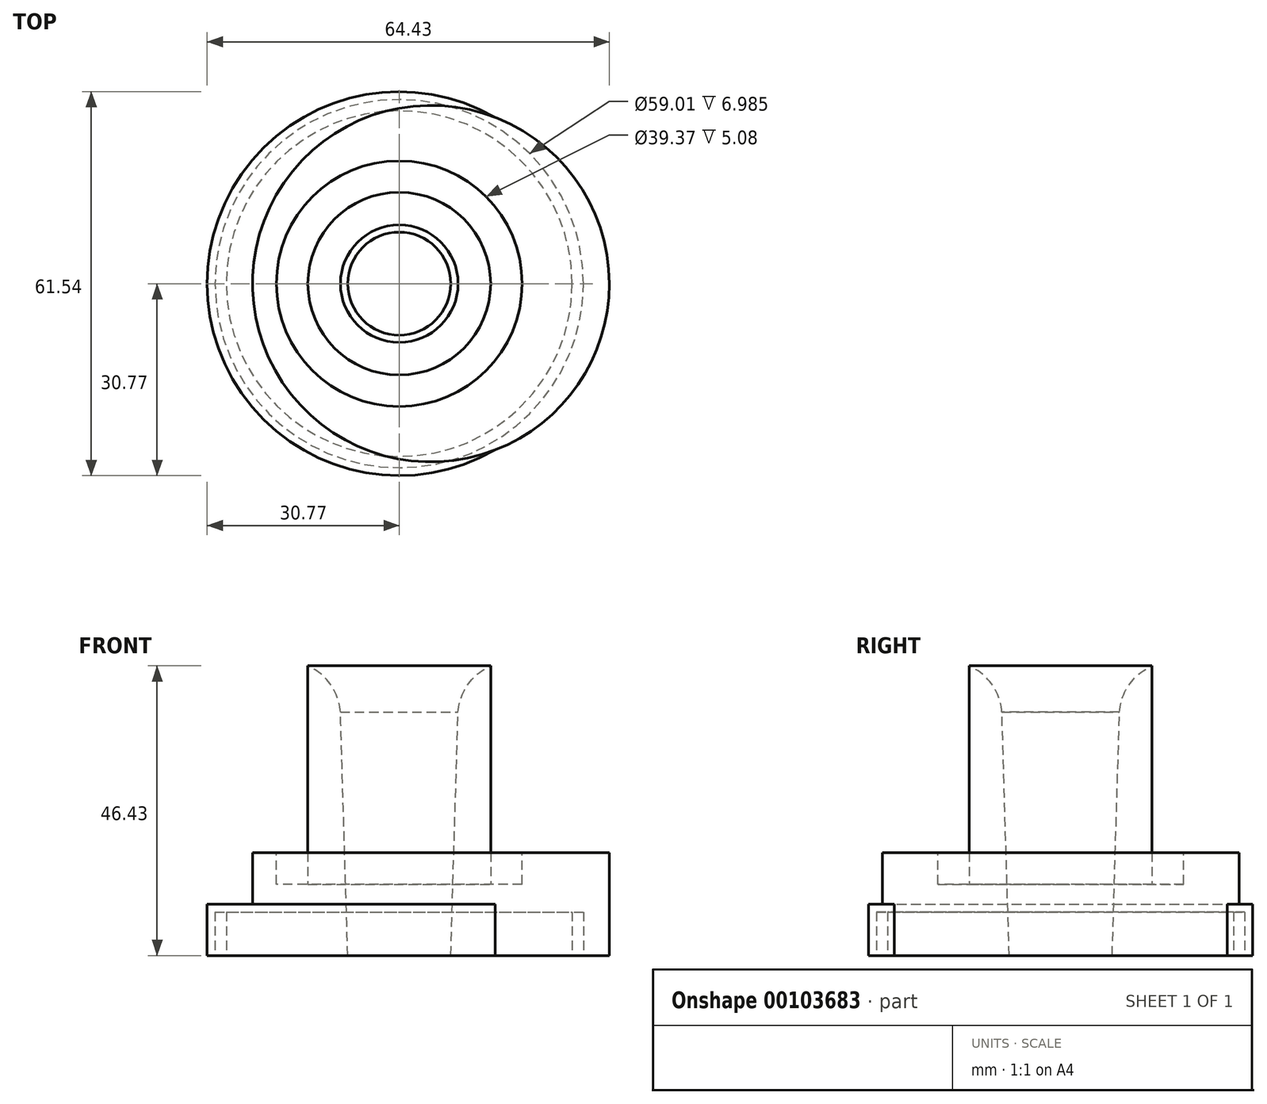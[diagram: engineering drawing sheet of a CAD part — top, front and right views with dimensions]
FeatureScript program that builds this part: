
annotation { "Feature Type Name" : "Feature", "Feature Type Description" : "" }
export const myFeature = defineFeature(function(context is Context, id is Id, definition is map)
    precondition{}
    {
        {
            var Q0;
            Q0=qCreatedBy(makeId("Front.planeOp"),FACE);
            var sketch = newSketch(context, id + "F0", { "sketchPlane" : qUnion([Q0])});
            skLineSegment(sketch, "E0", {"start": v(0, 0) * mm, "end": v(0, -8.25) * mm, "construction": true});
            skLineSegment(sketch, "E1", {"start": v(0, 0) * mm, "end": v(0, 38.1) * mm, "construction": true});
            skLineSegment(sketch, "E2", {"start": v(30.77, 0) * mm, "end": v(30.77, -8.26) * mm});
            skLineSegment(sketch, "E3", {"start": v(8.26, -8.25) * mm, "end": v(9.42, 30.76) * mm});
            skLineSegment(sketch, "E4", {"start": v(14.64, 38.17) * mm, "end": v(14.64, 0) * mm});
            skLineSegment(sketch, "E5.trimOffspring", {"start": v(14.64, 0) * mm, "end": v(30.77, 0) * mm});
            skLineSegment(sketch, "E6", {"start": v(27.72, -8.26) * mm, "end": v(27.72, -1.27) * mm});
            skLineSegment(sketch, "E7", {"start": v(27.72, -1.27) * mm, "end": v(29.5, -1.27) * mm});
            skLineSegment(sketch, "E8", {"start": v(29.5, -1.27) * mm, "end": v(29.5, -8.26) * mm});
            skLineSegment(sketch, "E9", {"start": v(8.26, -8.26) * mm, "end": v(27.72, -8.26) * mm});
            skLineSegment(sketch, "E10.trimOffspring", {"start": v(29.5, -8.26) * mm, "end": v(30.77, -8.26) * mm});
            skPoint(sketch, "E11.endSnap0", {"position": v(12.14, 38.1) * mm});
            skArc(sketch, "E12", {"start": v(14.64, 38.17) * mm, "mid": v(11, 35.2) * mm, "end": v(9.42, 30.76) * mm});
            skSolve(sketch);
        }
        {
            var Q0;
            Q0=makeQuery(id+"F0.imprint","IMPRINT",FACE,{"disambiguationData":[TD([[makeQuery(id+"F0.imprint","IMPRINT",EDGE,{"derivedFrom":sQuery(id+"F0.wireOp",EDGE,"E2")}),-1.0]])]});
            var Q1;
            Q1=sQuery(id+"F0.wireOp",EDGE,"E1");
            revolve(context, id + "F1", {"entities" : qUnion([Q0]), "axis" : qUnion([Q1]), "revolveType" : RevolveType.FULL});
        }
        {
            var Q0;
            Q0=makeQuery(id+"F1.opRevolve","SWEPT_FACE",FACE,{"disambiguationData":[OSD([sQuery(id+"F0.wireOp",EDGE,"E5.trimOffspring")])]});
            var sketch = newSketch(context, id + "F2", { "sketchPlane" : qUnion([Q0])});
            skCircle(sketch, "E13", {"center": v(5.08, 0) * mm, "radius": 28.58 * mm});
            skSolve(sketch);
        }
        {
            var Q0;
            {var subQ1=sQuery(id+"F0.wireOp",EDGE,"E5.trimOffspring");Q0=makeQuery(id+"F2.imprint","IMPRINT",FACE,{"disambiguationData":[TD([[makeQuery(id+"F2.imprint","IMPRINT",EDGE,{"derivedFrom":makeQuery(id+"F1.opRevolve","SWEPT_EDGE",EDGE,{"disambiguationData":[OSD([sQuery(id+"F0.wireOp",EDGE,"E4"),subQ1])]})}),1.0]])]});}
            var Q1;
            {var subQ0=sQuery(id+"F2.wireOp",EDGE,"E13");var subQ1=makeQuery(id+"F1.opRevolve","SWEPT_EDGE",EDGE,{"disambiguationData":[OSD([sQuery(id+"F0.wireOp",EDGE,"E2"),sQuery(id+"F0.wireOp",EDGE,"E5.trimOffspring")])]});var subQ2=makeQuery(id+"F2.imprint","INTERSECT",VERTEX,{"disambiguationData":[OD(0.0)],"derivedFrom":[subQ1,subQ0]});Q1=makeQuery(id+"F2.imprint","IMPRINT",FACE,{"disambiguationData":[TD([[makeQuery(id+"F2.imprint","IMPRINT",EDGE,{"disambiguationData":[TD([[subQ2,-1.0]])],"derivedFrom":subQ0}),1.0]])]});}
            extrude(context, id + "F3", {"entities" : qUnion([Q0, Q1]), "operationType" : NewBodyOperationType.ADD, "depth" : 8.25 * mm, "hasSecondDirection" : true, "secondDirectionOppositeDirection" : true, "secondDirectionDepth" : 8.25 * mm});
        }
        {
            var Q0;
            Q0=makeQuery(id+"F3.boolean.opBoolean","MERGE",FACE,{"derivedFrom":[makeQuery(id+"F1.opRevolve","SWEPT_FACE",FACE,{"disambiguationData":[OSD([sQuery(id+"F0.wireOp",EDGE,"E9")])]}),makeQuery(id+"F1.opRevolve","SWEPT_FACE",FACE,{"disambiguationData":[OSD([sQuery(id+"F0.wireOp",EDGE,"E10.trimOffspring")])]}),makeQuery(id+"F3.opExtrude","CAP_FACE",FACE,{"disambiguationData":[OSD([sQuery(id+"F0.wireOp",EDGE,"E4"),sQuery(id+"F0.wireOp",EDGE,"E5.trimOffspring"),sQuery(id+"F2.wireOp",EDGE,"E13")])],"isStart":true})]});
            var sketch = newSketch(context, id + "F4", { "sketchPlane" : qUnion([Q0])});
            skCircle(sketch, "E14", {"center": v(0, 0) * mm, "radius": 27.7 * mm});
            skCircle(sketch, "E15", {"center": v(0, 0) * mm, "radius": 29.5 * mm});
            skSolve(sketch);
        }
        {
            var Q0;
            Q0=makeQuery(id+"F4.imprint","IMPRINT",FACE,{"disambiguationData":[TD([[makeQuery(id+"F4.imprint","IMPRINT",EDGE,{"derivedFrom":sQuery(id+"F4.wireOp",EDGE,"E14")}),-1.0]])]});
            var Q1;
            Q1=sQuery(id+"F4.wireOp",EDGE,"E14");
            var Q2;
            Q2=sQuery(id+"F4.wireOp",EDGE,"E15");
            extrude(context, id + "F5", {"entities" : qUnion([Q0]), "operationType" : NewBodyOperationType.REMOVE, "surfaceEntities" : qUnion([Q1, Q2]), "oppositeDirection" : true, "depth" : 7 * mm});
        }
        {
            var Q0;
            Q0=makeQuery(id+"F3.opExtrude","CAP_FACE",FACE,{"disambiguationData":[OSD([sQuery(id+"F0.wireOp",EDGE,"E4"),sQuery(id+"F0.wireOp",EDGE,"E5.trimOffspring"),sQuery(id+"F2.wireOp",EDGE,"E13")])],"isStart":false});
            var sketch = newSketch(context, id + "F6", { "sketchPlane" : qUnion([Q0])});
            skCircle(sketch, "E16", {"center": v(0, 0) * mm, "radius": 19.69 * mm});
            skCircle(sketch, "E17", {"center": v(0, 0) * mm, "radius": 14.6 * mm});
            skSolve(sketch);
        }
        {
            var Q0;
            Q0=makeQuery(id+"F6.imprint","IMPRINT",FACE,{"disambiguationData":[TD([[makeQuery(id+"F6.imprint","IMPRINT",EDGE,{"derivedFrom":sQuery(id+"F6.wireOp",EDGE,"E16")}),1.0]])]});
            extrude(context, id + "F7", {"entities" : qUnion([Q0]), "operationType" : NewBodyOperationType.REMOVE, "oppositeDirection" : true, "depth" : 5.08 * mm});
        }
    });
